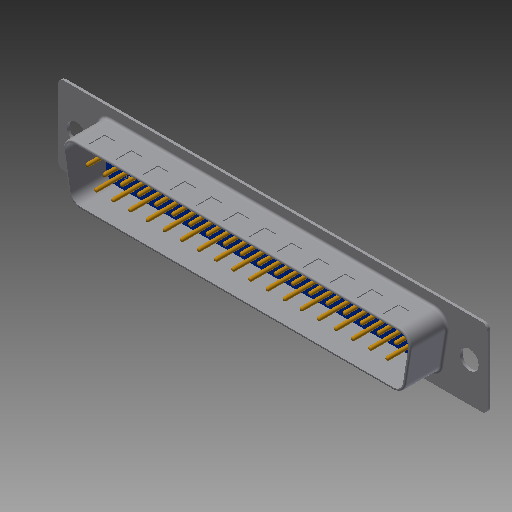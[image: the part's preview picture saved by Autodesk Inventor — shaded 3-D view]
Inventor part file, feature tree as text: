
AUTODESK INVENTOR PART (.ipt)
format: ipt  version: 2017 (Build 210142000, 142)  size: 565,760 bytes
history: native  units: in
note: dims shown in document units (in); Inventor stores cm internally (conversion verified against a paired STEP export)
features: extrude x1
ambient origin geometry x8: Origin, YZ Plane, XZ Plane, XY Plane, X Axis, Y Axis, Z Axis, Center Point
bodies: Solid1 (feature_tree)
feature tree (1):
  extrude  "Extrude11"  [1 undecoded]
note: 1 required parameter value undecoded (feature->parameter linkage not recoverable at this tier; creation-order binding heuristic only, values carry confidence <= 0.55)
